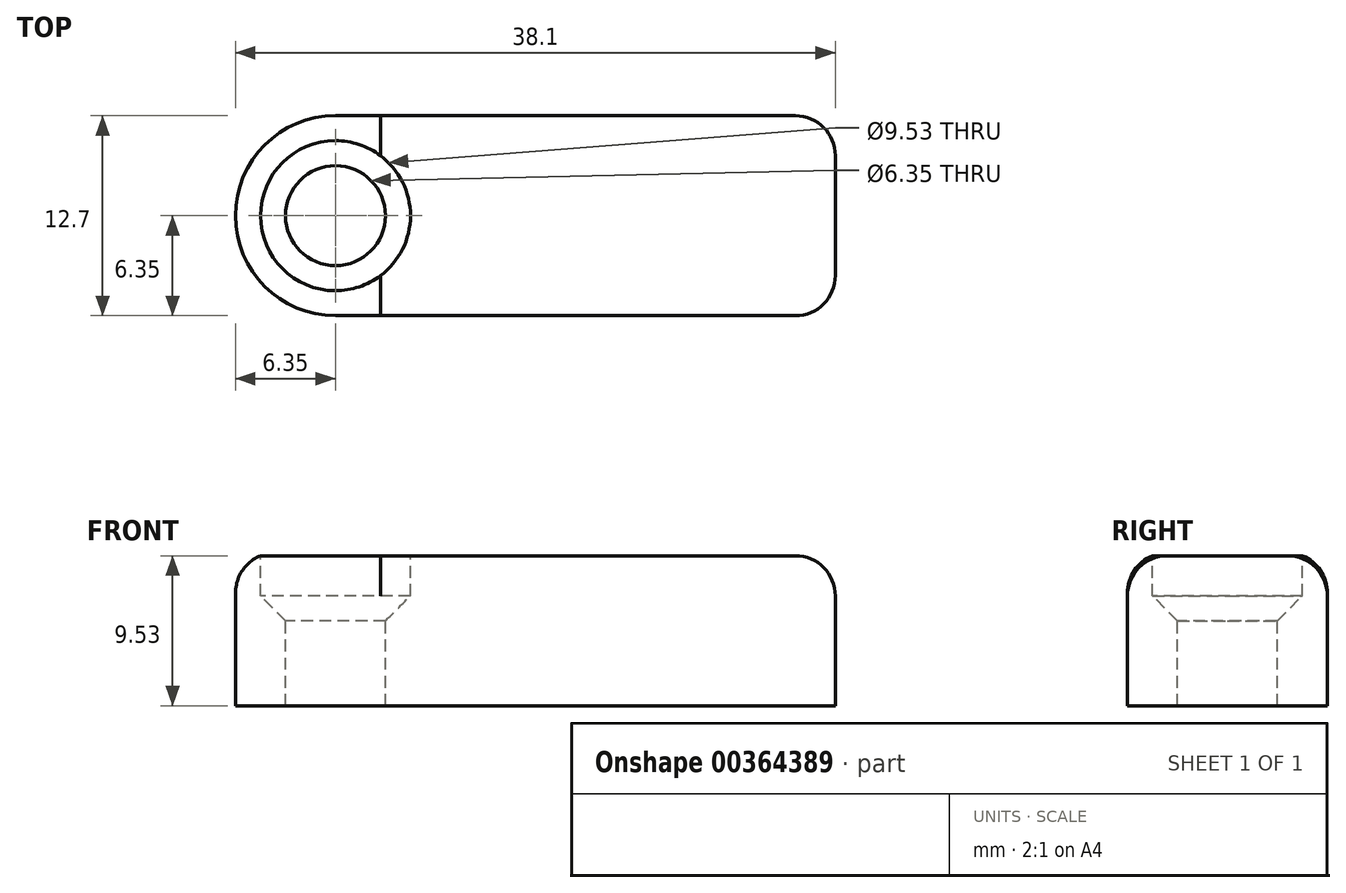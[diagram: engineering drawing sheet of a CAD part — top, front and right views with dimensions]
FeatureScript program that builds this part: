
annotation { "Feature Type Name" : "Feature", "Feature Type Description" : "" }
export const myFeature = defineFeature(function(context is Context, id is Id, definition is map)
    precondition{}
    {
        {
            var Q0;
            Q0=qCreatedBy(makeId("Top.planeOp"),FACE);
            var sketch = newSketch(context, id + "F0", { "sketchPlane" : qUnion([Q0])});
            skLineSegment(sketch, "E0.bottom", {"start": v(-12.7, -6.35) * mm, "end": v(19.05, -6.35) * mm});
            skLineSegment(sketch, "E0.top", {"start": v(-12.7, 6.35) * mm, "end": v(19.05, 6.35) * mm});
            skLineSegment(sketch, "E0.left", {"start": v(-19.05, -6.35) * mm, "end": v(-19.05, 6.35) * mm, "construction": true});
            skLineSegment(sketch, "E0.right", {"start": v(19.05, -6.35) * mm, "end": v(19.05, 6.35) * mm});
            skArc(sketch, "E1", {"start": v(-12.7, 6.35) * mm, "mid": v(-19.05, 0) * mm, "end": v(-12.7, -6.35) * mm});
            skSolve(sketch);
        }
        {
            var Q0;
            Q0=makeQuery(id+"F0.imprint","IMPRINT",FACE,{"disambiguationData":[TD([[makeQuery(id+"F0.imprint","IMPRINT",EDGE,{"derivedFrom":sQuery(id+"F0.wireOp",EDGE,"E0.bottom")}),1.0]])]});
            extrude(context, id + "F1", {"entities" : qUnion([Q0]), "depth" : 9.52 * mm});
        }
        {
            var Q0;
            Q0=qCreatedBy(makeId("Front.planeOp"),FACE);
            var sketch = newSketch(context, id + "F2", { "sketchPlane" : qUnion([Q0])});
            skLineSegment(sketch, "E2", {"start": v(-17.46, 9.53) * mm, "end": v(-17.46, 6.99) * mm});
            skLineSegment(sketch, "E3", {"start": v(-17.46, 6.99) * mm, "end": v(-15.88, 5.4) * mm});
            skLineSegment(sketch, "E4", {"start": v(-15.88, 5.4) * mm, "end": v(-15.88, 0) * mm});
            skLineSegment(sketch, "E5", {"start": v(-15.88, 0) * mm, "end": v(-12.7, 0) * mm});
            skLineSegment(sketch, "E6", {"start": v(-12.7, 0) * mm, "end": v(-12.7, 9.53) * mm});
            skLineSegment(sketch, "E7", {"start": v(-12.7, 9.53) * mm, "end": v(-17.46, 9.53) * mm});
            skSolve(sketch);
        }
        {
            var Q0;
            Q0 = qSketchRegion(id + "F2", true);
            var Q1;
            Q1=sQuery(id+"F2.wireOp",EDGE,"E5");
            var Q2;
            Q2=sQuery(id+"F2.wireOp",EDGE,"E6");
            revolve(context, id + "F3", {"operationType" : NewBodyOperationType.REMOVE, "entities" : qUnion([Q0]), "surfaceEntities" : qUnion([Q1]), "axis" : qUnion([Q2]), "revolveType" : RevolveType.FULL, "oppositeDirection" : true});
        }
        {
            var Q0;
            Q0=makeQuery(id+"F1.opExtrude","CAP_EDGE",EDGE,{"disambiguationData":[OSD([sQuery(id+"F0.wireOp",EDGE,"E0.bottom")])],"isStart":false});
            var Q1;
            Q1=makeQuery(id+"F1.opExtrude","CAP_EDGE",EDGE,{"disambiguationData":[OSD([sQuery(id+"F0.wireOp",EDGE,"E0.right")])],"isStart":false});
            var Q2;
            Q2=makeQuery(id+"F1.opExtrude","SWEPT_EDGE",EDGE,{"disambiguationData":[OSD([sQuery(id+"F0.wireOp",EDGE,"E0.bottom"),sQuery(id+"F0.wireOp",EDGE,"E0.right")])]});
            var Q3;
            Q3=makeQuery(id+"F1.opExtrude","SWEPT_EDGE",EDGE,{"disambiguationData":[OSD([sQuery(id+"F0.wireOp",EDGE,"E0.top"),sQuery(id+"F0.wireOp",EDGE,"E0.right")])]});
            fillet(context, id + "F4", {"entities" : qUnion([Q0, Q1, Q2, Q3]), "radius" : 2.54 * mm, "tangentPropagation" : true, "allowEdgeOverflow" : false});
        }
    });
